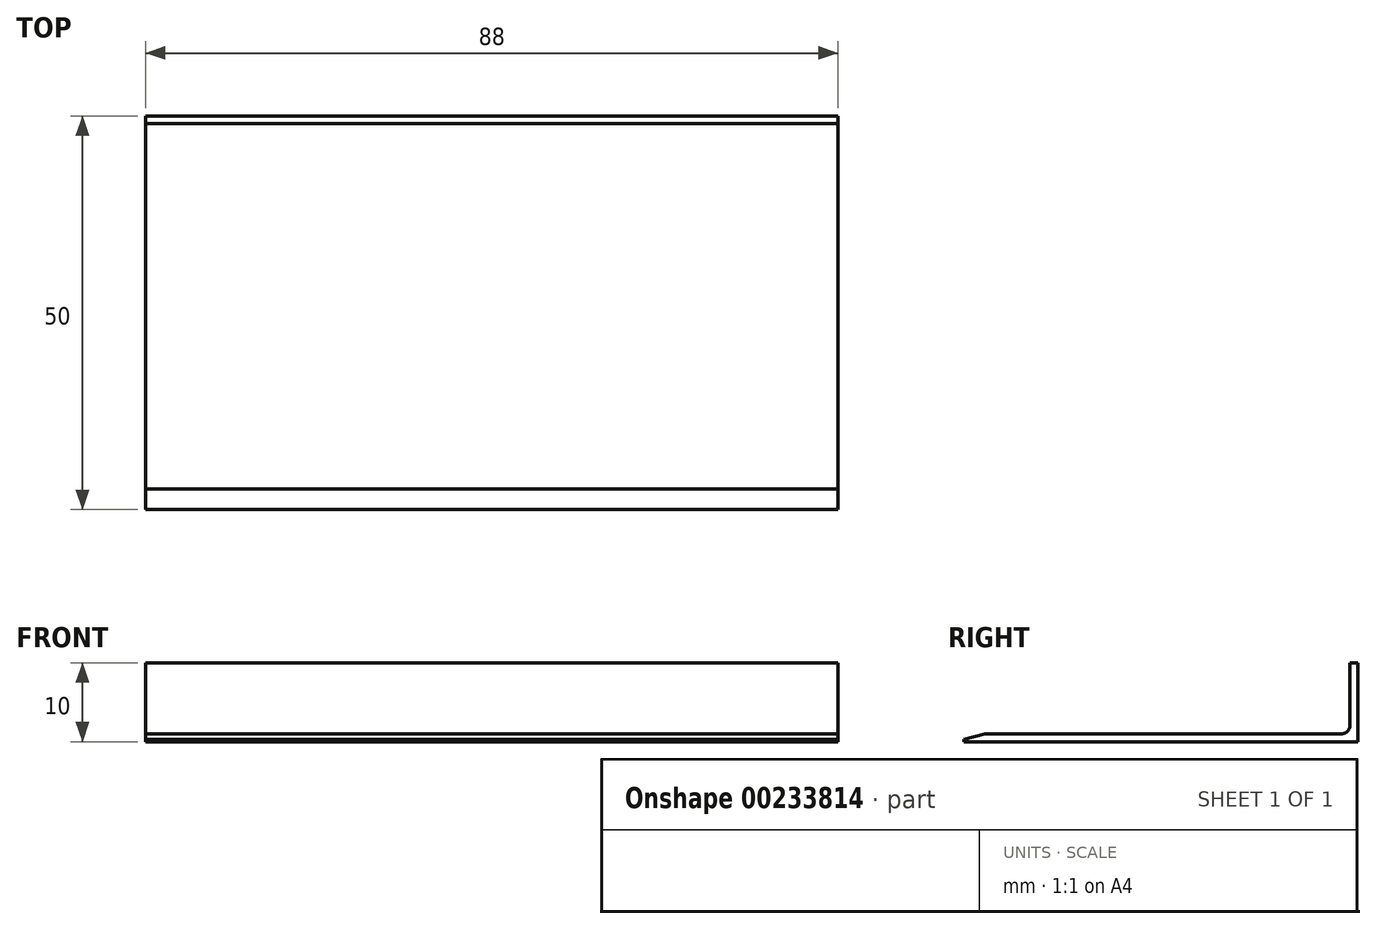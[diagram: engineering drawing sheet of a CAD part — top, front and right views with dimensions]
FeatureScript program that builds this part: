
annotation { "Feature Type Name" : "Feature", "Feature Type Description" : "" }
export const myFeature = defineFeature(function(context is Context, id is Id, definition is map)
    precondition{}
    {
        {
            var Q0;
            Q0=qCreatedBy(makeId("Right.planeOp"),FACE);
            var sketch = newSketch(context, id + "F0", { "sketchPlane" : qUnion([Q0])});
            skLineSegment(sketch, "E0", {"start": v(-50, 0) * mm, "end": v(-50, 0.3) * mm});
            skLineSegment(sketch, "E1", {"start": v(-50, 0.3) * mm, "end": v(-47.39, 1) * mm});
            skLineSegment(sketch, "E2", {"start": v(-47.39, 1) * mm, "end": v(-2, 1) * mm});
            skLineSegment(sketch, "E3", {"start": v(-1, 2) * mm, "end": v(-1, 10) * mm});
            skLineSegment(sketch, "E4", {"start": v(-1, 10) * mm, "end": v(0, 10) * mm});
            skLineSegment(sketch, "E5", {"start": v(0, 10) * mm, "end": v(0, 0) * mm});
            skLineSegment(sketch, "E6", {"start": v(0, 0) * mm, "end": v(-50, 0) * mm});
            skLineSegment(sketch, "E7", {"start": v(-1, 10) * mm, "end": v(-10, 1) * mm, "construction": true});
            skPoint(sketch, "E8.visualSharp", {"position": v(-1, 1) * mm});
            skArc(sketch, "E8.filletArc", {"start": v(-2, 1) * mm, "mid": v(-1.3, 1.3) * mm, "end": v(-1, 2) * mm});
            skSolve(sketch);
        }
        {
            var Q0;
            Q0 = qSketchRegion(id + "F0", true);
            extrude(context, id + "F1", {"entities" : qUnion([Q0]), "depth" : 88 * mm});
        }
    });
